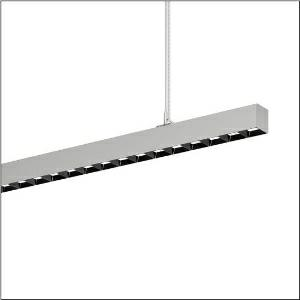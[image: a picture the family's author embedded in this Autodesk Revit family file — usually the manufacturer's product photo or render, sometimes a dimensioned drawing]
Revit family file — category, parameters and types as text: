
# Revit family: silica_r__21_51mx32dc3dsb_c9e6
name_source: partatom
category: Lighting Fixtures
units: mm (PartAtom-declared; Revit-internal decimal feet)

## family parameters
Cut with Voids When Loaded = No
Host = Face
Light Source = No
Part Type = Normal
Room Calculation Point = No
Round Connector Dimension = Use Diameter
Shared = No

## types (1)
- --- (1 x LED, 18220 lm, 113 W, 3000K)
    Apparent Load = 113 VA
    CIE Flux Codes = 86 99 100 59 100
    Color Rendering = 80
    Color Temperature = 3000K
    Default Elevation = 1800 mm
    Description = Silica® 21, office luminaire, primary light control with darklight reflector, of PMMA, black, CAT 2 (L<= 3000cd/m²), light emission: direct/indirect distribution, primary light characteristic: symmetric, installation type: suspended mounting, LED, rated luminous flux: 18.220lm, luminous efficacy: 161lm/W, light colour: 830, colour temperature: 3000K, control gear: DALI 2, with terminal, 3+2-pole, max. 2.5mm², mains connection: 220..240V, AC, 50/60Hz, rated input power: 113W, luminaire housing, of aluminium, metallic grey (RAL 9006), length: 3.004mm, width: 53mm, height: 53mm, protection rating (complete): IP20, insulation class (complete): insulation class I (protective earthing), certification: CE, permissible operating ambient temperature: 0..+35°C, standard: EN 50419, packaging unit: 1 piece
    Height = 53 mm
    Lamp = 1 x LED
    Lamp Light Flux = 18220 lm
    Lamp Power = 113 W
    Lamp count = 1
    Length = 3004 mm
    Luminous efficacy = 161 lm/W
    Manufacturer = Siteco
    ModVariant = No
    Model = 51MX32DC3DSB
    Mounting Place = Ceiling
    Mounting Type = Pendant
    Number of Poles = 1
    OnlyDefault = Yes
    Power Factor = 1
    Product Name = Silica® 21
    Product group = office luminaire | ceiling pendant
    ProductGroupID = 903
    Protection Class = Protection class I
    Protection Degree = IP 20
    RLX_Detail_Level = 1
    RLX_Emergency_Light_Flux = 0 lm
    RLX_Emergency_Type = 0
    RLX_Emergency_Type_DB = No
    RlxData = <blob elided: 65085 chars, md5=7c3a3621>
    Socket = socket
    Standby Power = 0 W
    System Light Flux = 18220 lm
    System Power = 113 W
    Type Comments = factory setting: luminous flux: 100 % | dim-lin: 254 | 391 mA
    Type Image = l_1335859.jpg
    URL = http://relux.com
    VarID = @adj_143463
    Voltage = 0 V
    Weight = 0.00 kg
    Width = 53 mm

## geometry (parser evidence)
native form markers: Blend x4, Sweep x13
no freeform markers — native parametric forms only
